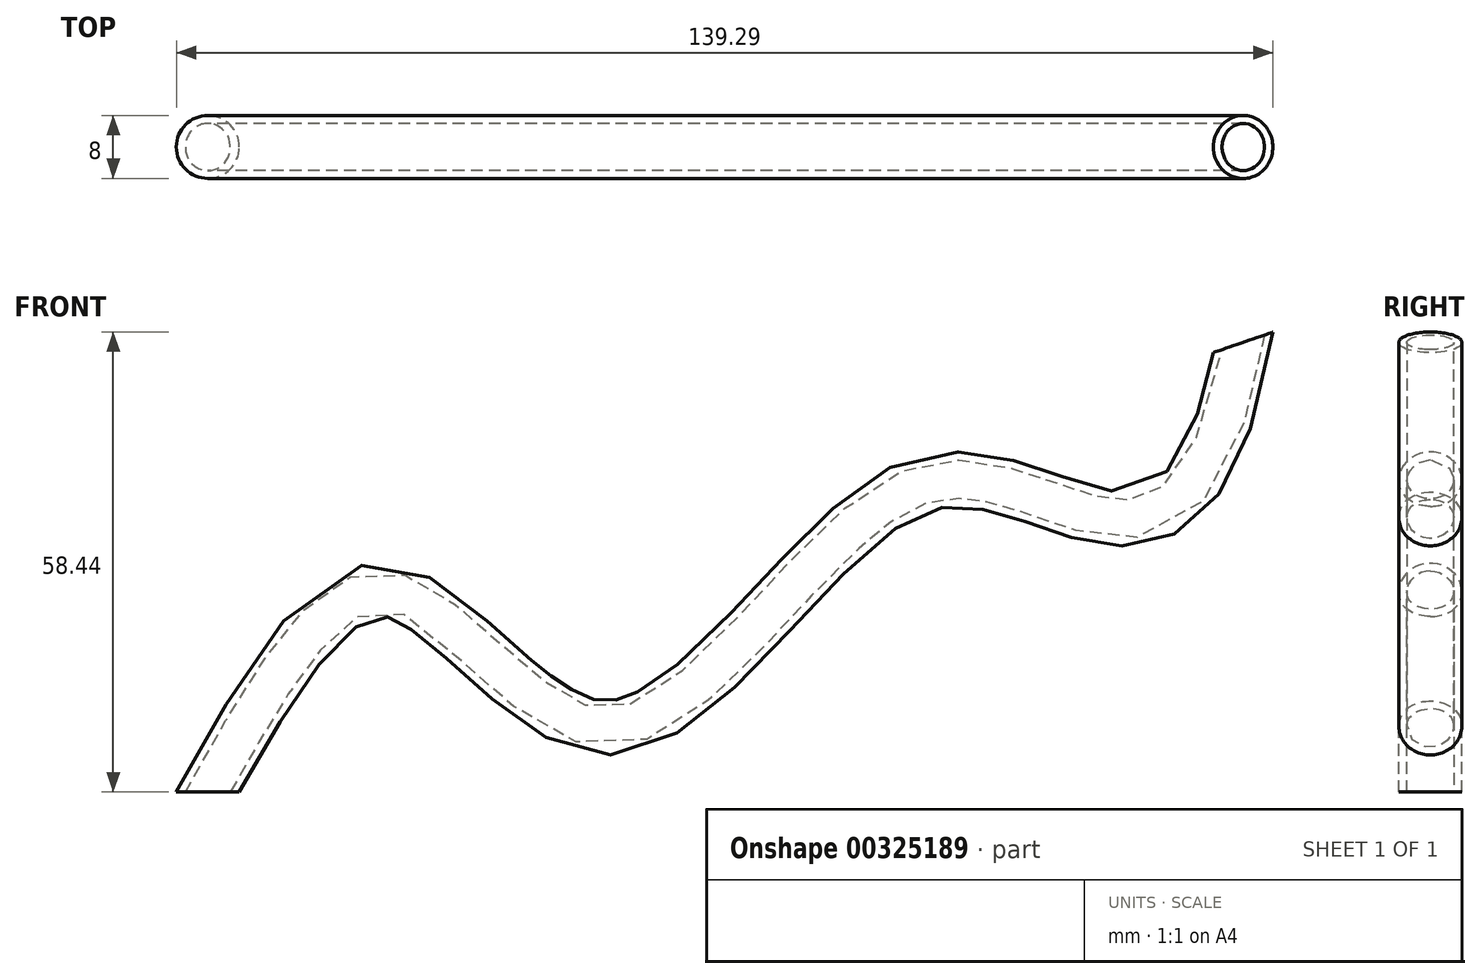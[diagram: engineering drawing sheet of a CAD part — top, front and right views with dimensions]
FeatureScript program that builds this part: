
annotation { "Feature Type Name" : "Feature", "Feature Type Description" : "" }
export const myFeature = defineFeature(function(context is Context, id is Id, definition is map)
    precondition{}
    {
        {
            var Q0;
            Q0=qCreatedBy(makeId("Front.planeOp"),FACE);
            var sketch = newSketch(context, id + "F0", { "sketchPlane" : qUnion([Q0])});
            skFitSpline(sketch, "E0", {"points": [v(-62.88, 0) * mm, v(-39.08, 25.2) * mm, v(-11.7, 8.33) * mm, v(25.99, 38.28) * mm, v(50.08, 35.18) * mm, v(68.63, 57.13) * mm], "startDerivative": vector(122.15, 218.12) * mm, "endDerivative": vector(58, 324.29) * mm});
            skSolve(sketch);
        }
        {
            var Q0;
            Q0=qCreatedBy(makeId("Top.planeOp"),FACE);
            var sketch = newSketch(context, id + "F1", { "sketchPlane" : qUnion([Q0])});
            skCircle(sketch, "E1", {"center": v(-62.88, 0) * mm, "radius": 4 * mm});
            skSolve(sketch);
        }
        {
            var Q0;
            Q0=makeQuery(id+"F1.imprint","IMPRINT",FACE,{"disambiguationData":[TD([[makeQuery(id+"F1.imprint","IMPRINT",EDGE,{"derivedFrom":sQuery(id+"F1.wireOp",EDGE,"E1")}),1.0]])]});
            var Q1;
            Q1=sQuery(id+"F0.wireOp",EDGE,"E0");
            sweep(context, id + "F2", {"profiles" : qUnion([Q0]), "path" : qUnion([Q1])});
        }
        {
            var Q0;
            Q0=makeQuery(id+"F2.opSweep","CAP_FACE",FACE,{"disambiguationData":[OSD([sQuery(id+"F0.wireOp",VERTEX,"E0.start"),sQuery(id+"F1.wireOp",EDGE,"E1")])],"isStart":true});
            var Q1;
            Q1=makeQuery(id+"F2.opSweep","CAP_FACE",FACE,{"disambiguationData":[OSD([sQuery(id+"F0.wireOp",VERTEX,"E0.end"),sQuery(id+"F1.wireOp",EDGE,"E1")])],"isStart":false});
            var Q2;
            Q2=makeQuery(id+"F2.opSweep","CAP_FACE",FACE,{"disambiguationData":[OSD([sQuery(id+"F0.wireOp",VERTEX,"E0.end"),sQuery(id+"F1.wireOp",EDGE,"E1")])],"isStart":false});
            shell(context, id + "F3", {"entities" : qUnion([Q0, Q1, Q2]), "thickness" : 1 * mm});
        }
    });
